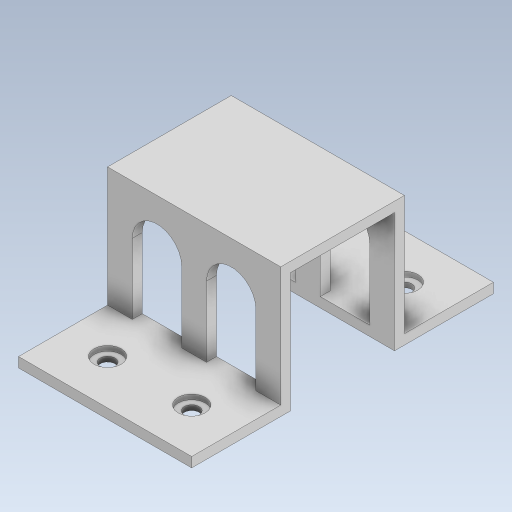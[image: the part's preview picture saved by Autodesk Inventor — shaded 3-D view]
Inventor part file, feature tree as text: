
AUTODESK INVENTOR PART (.ipt)
format: ipt  version: 2023.5 (Build 275446000, 446)  size: 216,064 bytes
history: native  units: in
note: dims shown in document units (in); Inventor stores cm internally (conversion verified against a paired STEP export)
features: extrude x10, sketch x8
ambient origin geometry x8: Origin, YZ Plane, XZ Plane, XY Plane, X Axis, Y Axis, Z Axis, Center Point
bodies: Solid1 (feature_tree)
feature tree (18):
  extrude  "Extrusion1"  Depth=0.7874in
  extrude  "Extrusion2"  Depth=0.0787in
  extrude  "Extrusion3"  Depth=0.0787in
  extrude  "Extrusion4"  Depth=0.0787in
  extrude  "Extrusion5"  Depth=0.7087in TaperAngle=0.0deg
  sketch  "Sketch6"  dims[d15=0.1181in d16=0.3543in]
  extrude  "Extrusion6"  Depth=0.3543in
  extrude  "Extrusion7"  Depth=0.1181in
  sketch  "Sketch7"  dims[d17=0.3543in d18=0.1181in]
  extrude  "Extrusion8"  Depth=0.9843in
  extrude  "Extrusion9"  Depth=0.9843in
  extrude  "Extrusion10"  Depth=0.0787in TaperAngle=0.0deg
  sketch  "Sketch1"  dims[d0=1.378in d1=0.7874in]
  sketch  "Sketch2"  dims[d2=0.0787in d3=0.0in d4=0.0787in]
  sketch  "Sketch3"  dims[d5=0.9528in d6=0.0in d7=0.0787in]
  sketch  "Sketch4"  dims[d8=0.9055in d9=0.0in d10=0.0787in]
  sketch  "Sketch5"  dims[d11=0.9528in d12=0.0in d13=0.7087in d14=0.0in]
  sketch  "Sketch8"  dims[d19=0.6693in d20=0.2165in d21=0.2165in d22=0.0787in d23=0.0in d24=0.0394in d25=0.0in d26=0.1181in d27=0.3543in d28=0.3543in d29=0.1181in d30=0.6693in d31=0.2165in d32=0.2165in d33=0.0787in d34=0.0in d35=0.0394in d36=0.0in d37=0.3937in d38=0.3937in d39=0.3937in d40=0.9843in d41=0.0in]
